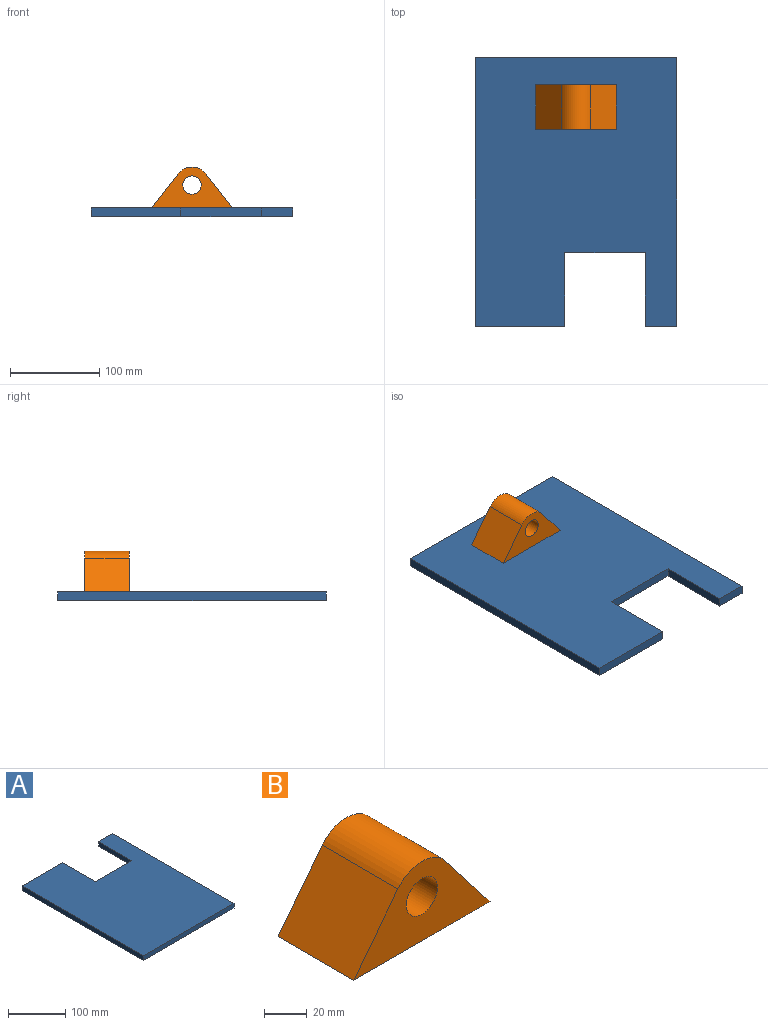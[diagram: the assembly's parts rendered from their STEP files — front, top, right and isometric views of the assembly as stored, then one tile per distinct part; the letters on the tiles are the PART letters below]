
ASSEMBLY  parts=2 mates=1
PART A: 10 faces, bbox 225x300x10 mm
  f0: plane 100x10mm, normal (0,1,0), area 1000mm2, adj f1,f7,f8,f9
  f1: plane 82x10mm, normal (1,0,0), area 820mm2, adj f0,f2,f8,f9
  f2: plane 90x10mm, normal (0,1,0), area 900mm2, adj f1,f3,f8,f9
  f3: plane 82x10mm, normal (-1,0,0), area 820mm2, adj f2,f4,f8,f9
  f4: plane 35x10mm, normal (0,1,0), area 350mm2, adj f3,f5,f8,f9
  f5: plane 300x10mm, normal (1,0,0), area 3000mm2, adj f4,f6,f8,f9
  f6: plane 225x10mm, normal (0,-1,0), area 2250mm2, adj f5,f7,f8,f9
  f7: plane 300x10mm, normal (-1,0,0), area 3000mm2, adj f0,f6,f8,f9
  f8: plane 300x225mm, normal (0,0,-1), area 60120mm2, adj f0,f1,f2,f3,f4,f5,f6,f7
  f9: plane 300x225mm, normal (0,0,1), area 60120mm2, adj f0,f1,f2,f3,f4,f5,f6,f7
PART B: 7 faces, bbox 90x50x45.5 mm
  f0: cylinder r=20mm len=50mm, axis (0,1,0), area 1825.1mm2, adj f1,f4,f5,f6
  f1: plane 50x37.73mm, normal (-0.79,0,0.61), area 2385mm2, adj f0,f2,f5,f6
  f2: plane 90x50mm, normal (0,0,-1), area 4500mm2, adj f1,f4,f5,f6
  f3: cylinder r=10.25mm len=50mm, axis (0,1,0), area 3220.1mm2, adj f5,f6
  f4: plane 50x37.73mm, normal (0.79,0,0.61), area 2385mm2, adj f0,f2,f5,f6
  f5: plane 90x45.5mm, normal (0,-1,0), area 2136.5mm2, adj f0,f1,f2,f3,f4
  f6: plane 90x45.5mm, normal (0,1,0), area 2136.5mm2, adj f0,f1,f2,f3,f4
PLACE A rot(axis=(1,0,0),180deg) t=(-2.57,81.5,1547.99)mm
PLACE B t=(-32.87,429.5,-5.01)mm
MATE fastened A.f8 <-> B.f2  axis (0,0,1) through (-35.07,459.5,774.99)mm
